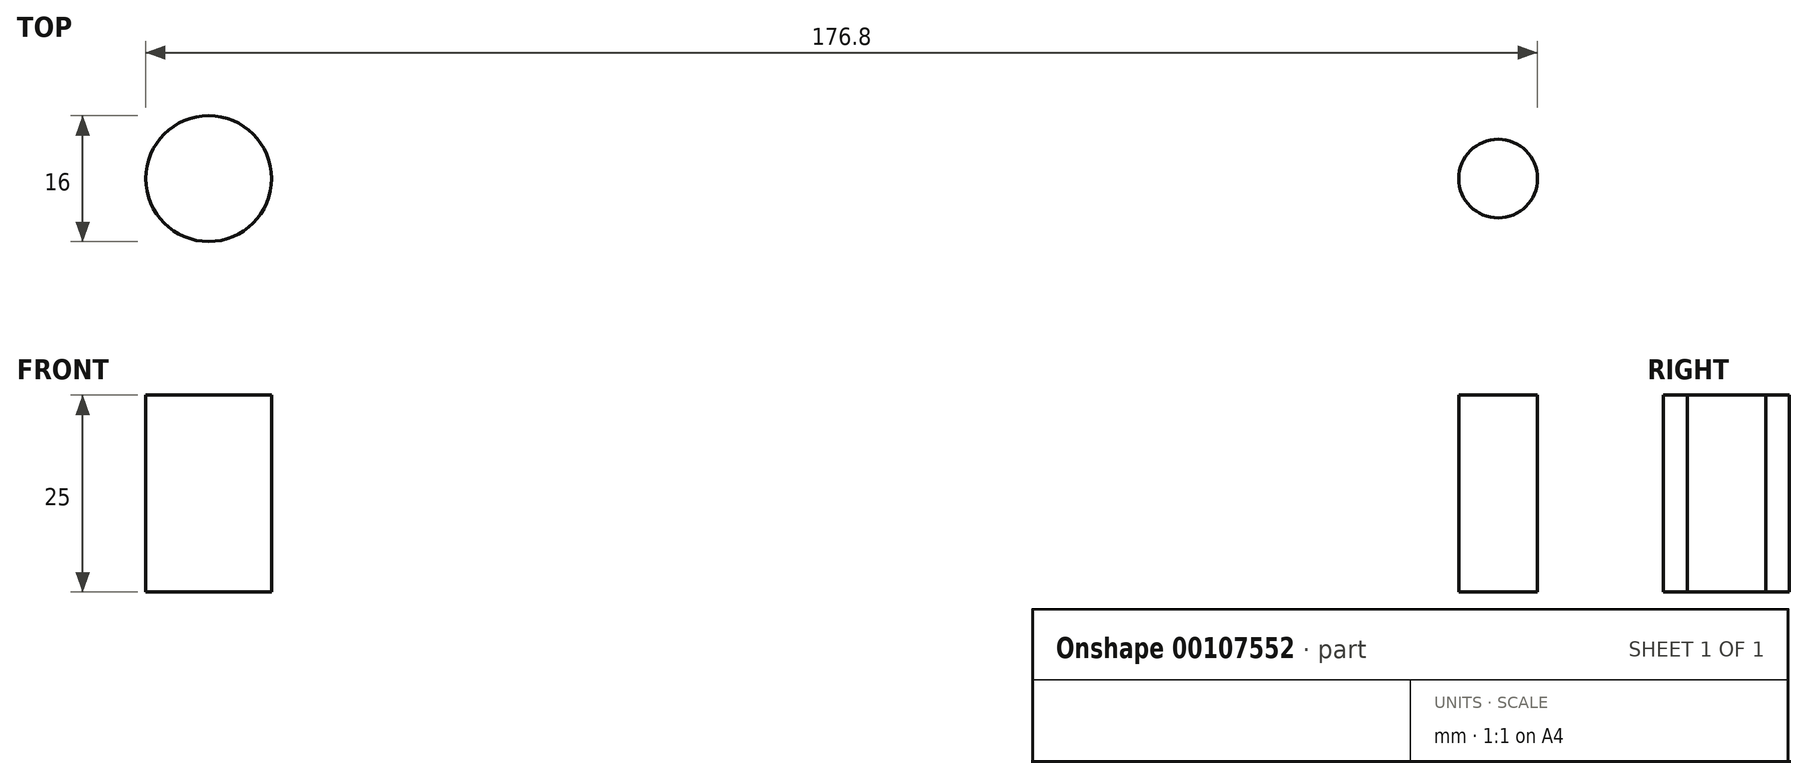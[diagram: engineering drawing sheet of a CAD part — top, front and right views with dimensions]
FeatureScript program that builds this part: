
annotation { "Feature Type Name" : "Feature", "Feature Type Description" : "" }
export const myFeature = defineFeature(function(context is Context, id is Id, definition is map)
    precondition{}
    {
        {
            var Q0;
            Q0=qCreatedBy(makeId("Top.planeOp"),FACE);
            var sketch = newSketch(context, id + "F0", { "sketchPlane" : qUnion([Q0])});
            skCircle(sketch, "E0", {"center": v(0, 0) * mm, "radius": 8 * mm});
            skCircle(sketch, "E1", {"center": v(163.8, 0) * mm, "radius": 5 * mm});
            skSolve(sketch);
        }
        {
            var Q0;
            Q0=qSketchRegion(id+"F0",true);
            extrude(context, id + "F1", {"entities" : qUnion([Q0]), "endBound" : BoundingType.SYMMETRIC, "depth" : 25 * mm});
        }
    });
